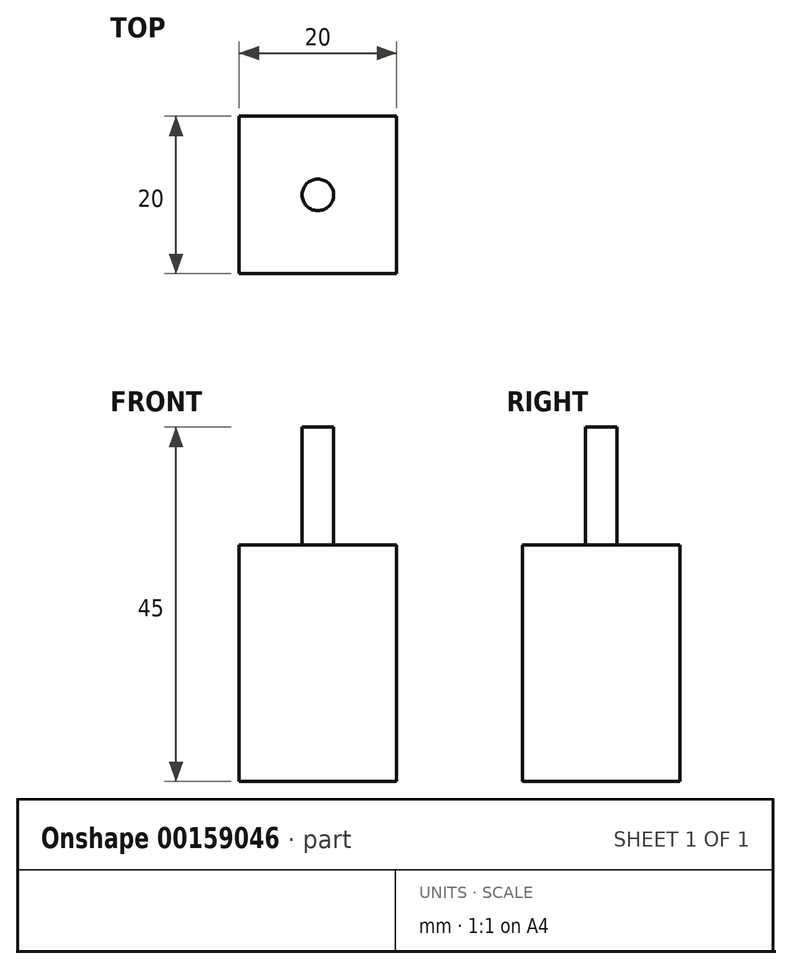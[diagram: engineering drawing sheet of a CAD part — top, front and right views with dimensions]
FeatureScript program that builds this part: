
annotation { "Feature Type Name" : "Feature", "Feature Type Description" : "" }
export const myFeature = defineFeature(function(context is Context, id is Id, definition is map)
    precondition{}
    {
        {
            var Q0;
            Q0=qCreatedBy(makeId("Top.planeOp"),FACE);
            var sketch = newSketch(context, id + "F0", { "sketchPlane" : qUnion([Q0])});
            skLineSegment(sketch, "E0.bottom", {"start": v(10, 10) * mm, "end": v(-10, 10) * mm});
            skLineSegment(sketch, "E0.top", {"start": v(10, -10) * mm, "end": v(-10, -10) * mm});
            skLineSegment(sketch, "E0.left", {"start": v(10, 10) * mm, "end": v(10, -10) * mm});
            skLineSegment(sketch, "E0.right", {"start": v(-10, 10) * mm, "end": v(-10, -10) * mm});
            skPoint(sketch, "E0.middle", {"position": v(0, 0) * mm});
            skSolve(sketch);
        }
        {
            var Q0;
            Q0 = qSketchRegion(id + "F0", true);
            extrude(context, id + "F1", {"entities" : qUnion([Q0]), "depth" : 30 * mm});
        }
        {
            var Q0;
            Q0=makeQuery(id+"F1.opExtrude","CAP_FACE",FACE,{"disambiguationData":[OSD([sQuery(id+"F0.wireOp",EDGE,"E0.bottom"),sQuery(id+"F0.wireOp",EDGE,"E0.top"),sQuery(id+"F0.wireOp",EDGE,"E0.left"),sQuery(id+"F0.wireOp",EDGE,"E0.right")])],"isStart":false});
            var sketch = newSketch(context, id + "F2", { "sketchPlane" : qUnion([Q0])});
            skCircle(sketch, "E1", {"center": v(0, 0) * mm, "radius": 2 * mm});
            skSolve(sketch);
        }
        {
            var Q0;
            Q0 = qSketchRegion(id + "F2", true);
            extrude(context, id + "F3", {"entities" : qUnion([Q0]), "operationType" : NewBodyOperationType.ADD, "depth" : 15 * mm});
        }
    });
